# Revit family: Keilhauer_Juxta_Table_050114
name_source: partatom
category: Furniture
units: mm (PartAtom-declared; Revit-internal decimal feet)

## family parameters
Always vertical = Yes
Cut with Voids When Loaded = No
OmniClass Number = 23.40.70.14.64.11
OmniClass Title = Office Furniture
Room Calculation Point = No
Shared = No
Work Plane-Based = No

## types (27) — shared parameters
Assembly Code = E2020200
Leg Radius = 0.5 "
Manufacturer = Keilhauer, Corp.
Product Documentation Link = http://www.keilhauer.com
URL = http://www.keilhauer.com
zero-valued in all types: Default Elevation

## per-type parameters (varying)
| type | Diameter | Height | Leg Big | Leg Height | Leg Length | Leg Small | Model | Round | Square | Support |
| 30" Round Table Occasional Height | 30 " | 15 " | No | 1.58 " | 13.22 " | Yes | 47231 | Yes | No | No |
| 30" Round Table Lounge Height | 30 " | 26 " | No | 1.58 " | 13.22 " | Yes | 47232 | Yes | No | No |
| 30" Round Table Conference Height | 30 " | 29 " | No | 1.58 " | 13.22 " | Yes | 47233 | Yes | No | No |
| 30" Round Table Counter Height | 30 " | 36 " | No | 1.58 " | 13.22 " | Yes | 47234 | Yes | No | Yes |
| 30" Round Table Bar Height | 30 " | 41.75 " | No | 1.58 " | 13.22 " | Yes | 47235 | Yes | No | Yes |
| 36" Round Table Bar Height | 36 " | 41.75 " | No | 1.58 " | 13.22 " | Yes | 47245 | Yes | No | Yes |
| 36" Round Table Conference Height | 36 " | 29 " | No | 1.58 " | 13.22 " | Yes | 47243 | Yes | No | No |
| 36" Round Table Counter Height | 36 " | 36 " | No | 1.58 " | 13.22 " | Yes | 47244 | Yes | No | Yes |
| 36" Round Table Lounge Height | 36 " | 26 " | No | 1.58 " | 13.22 " | Yes | 47242 | Yes | No | No |
| 36" Round Table Occasional Height | 36 " | 15 " | No | 1.58 " | 13.22 " | Yes | 47241 | Yes | No | No |
| 42" Round Table Occasional Height | 42 " | 15 " | No | 1.58 " | 13.22 " | Yes | 47251 | Yes | No | No |
| 42" Round Table Lounge Height | 42 " | 26 " | No | 1.58 " | 13.22 " | Yes | 47252 | Yes | No | No |
| 42" Round Table Conference Height | 42 " | 29 " | No | 1.58 " | 13.22 " | Yes | 47253 | Yes | No | No |
| 48" Round Table Lounge Height | 48 " | 26 " | Yes | 1.435 " | 18.296 " | No | 47262 | Yes | No | No |
| 48" Round Table Conference Height | 48 " | 29 " | Yes | 1.435 " | 18.296 " | No | 47263 | Yes | No | No |
| 30" Square Table Occasional Height | 30 " | 15 " | No | 1.58 " | 13.22 " | Yes | 47131 | No | Yes | No |
| 30" Square Table Lounge Height | 30 " | 26 " | No | 1.58 " | 13.22 " | Yes | 47132 | No | Yes | No |
| 30" Square Table Conference Height | 30 " | 29 " | No | 1.58 " | 13.22 " | Yes | 47133 | No | Yes | No |
| 30" Square Table Bar Height | 30 " | 41.75 " | No | 1.58 " | 13.22 " | Yes | 47135 | No | Yes | Yes |
| 30" Square Table Counter Height | 30 " | 36 " | No | 1.58 " | 13.22 " | Yes | 47134 | No | Yes | Yes |
| 36" Square Table Bar Height | 36 " | 41.75 " | No | 1.58 " | 13.22 " | Yes | 47145 | No | Yes | Yes |
| 36" Square Table Conference Height | 36 " | 29 " | No | 1.58 " | 13.22 " | Yes | 47143 | No | Yes | No |
| 36" Square Table Counter Height | 36 " | 36 " | No | 1.58 " | 13.22 " | Yes | 47144 | No | Yes | Yes |
| 36" Square Table Lounge Height | 36 " | 26 " | No | 1.58 " | 13.22 " | Yes | 47142 | No | Yes | No |
| 36" Square Table Occasional Height | 36 " | 15 " | No | 1.58 " | 13.22 " | Yes | 47141 | No | Yes | No |
| 48" Square Table Conference Height | 48 " | 29 " | Yes | 1.435 " | 18.296 " | No | 47163 | No | Yes | No |
| 48" Square Table Lounge Height | 48 " | 26 " | Yes | 1.435 " | 18.296 " | No | 47162 | No | Yes | No |

note: column(s) folded — value = type name in every type: Description

## geometry (parser evidence)
native form markers: Sweep x4
no freeform markers — native parametric forms only
